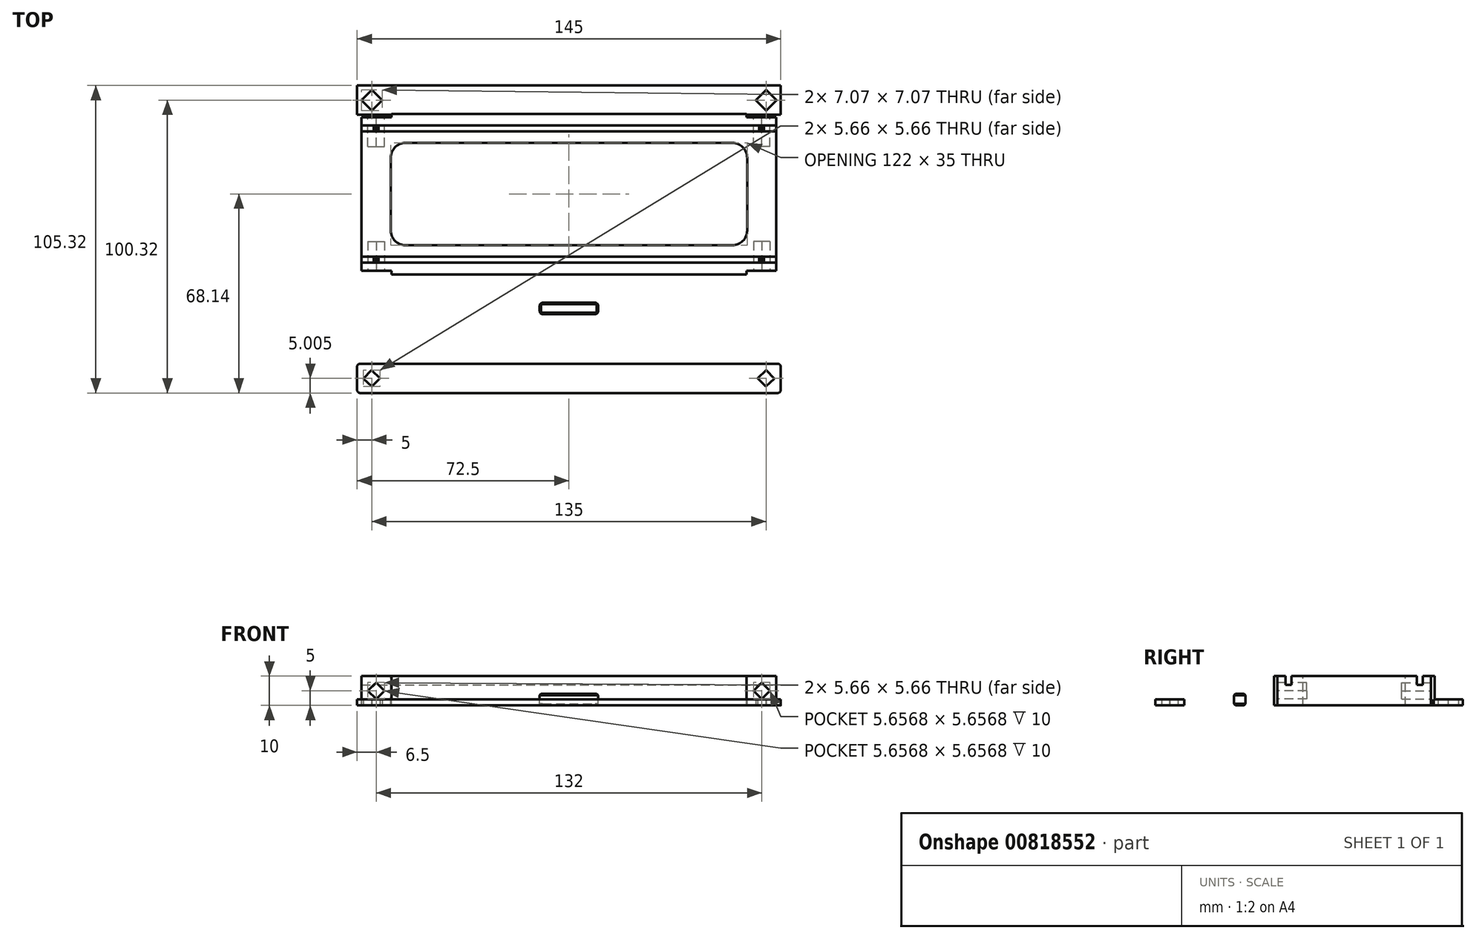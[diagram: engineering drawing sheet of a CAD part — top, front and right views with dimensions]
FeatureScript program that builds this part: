
annotation { "Feature Type Name" : "Feature", "Feature Type Description" : "" }
export const myFeature = defineFeature(function(context is Context, id is Id, definition is map)
    precondition{}
    {
        {
            var Q0;
            Q0=qCreatedBy(makeId("Top.planeOp"),FACE);
            var sketch = newSketch(context, id + "F0", { "sketchPlane" : qUnion([Q0])});
            skLineSegment(sketch, "E0.bottom", {"start": v(71, -27.5) * mm, "end": v(-71, -27.5) * mm});
            skLineSegment(sketch, "E0.top", {"start": v(71, 27.5) * mm, "end": v(-71, 27.5) * mm});
            skLineSegment(sketch, "E0.left", {"start": v(71, -27.5) * mm, "end": v(71, 27.5) * mm});
            skLineSegment(sketch, "E0.right", {"start": v(-71, -27.5) * mm, "end": v(-71, 27.5) * mm});
            skPoint(sketch, "E0.middle", {"position": v(0, 0) * mm});
            skSolve(sketch);
        }
        {
            var Q0;
            Q0 = qSketchRegion(id + "F0", true);
            extrude(context, id + "F1", {"entities" : qUnion([Q0]), "depth" : 10 * mm, "offsetDistance" : 25 * mm});
        }
        {
            var Q0;
            Q0=makeQuery(id+"F1.opExtrude","CAP_FACE",FACE,{"disambiguationData":[OSD([sQuery(id+"F0.wireOp",EDGE,"E0.bottom"),sQuery(id+"F0.wireOp",EDGE,"E0.top"),sQuery(id+"F0.wireOp",EDGE,"E0.left"),sQuery(id+"F0.wireOp",EDGE,"E0.right")])],"isStart":false});
            var sketch = newSketch(context, id + "F2", { "sketchPlane" : qUnion([Q0])});
            skLineSegment(sketch, "E1.bottom", {"start": v(-71, 23.5) * mm, "end": v(71, 23.5) * mm});
            skLineSegment(sketch, "E1.top", {"start": v(-71, 21.5) * mm, "end": v(71, 21.5) * mm});
            skLineSegment(sketch, "E1.left", {"start": v(-71, 23.5) * mm, "end": v(-71, 21.5) * mm});
            skLineSegment(sketch, "E1.right", {"start": v(71, 23.5) * mm, "end": v(71, 21.5) * mm});
            skLineSegment(sketch, "E2.MirrorCS", {"start": v(71, -23.5) * mm, "end": v(71, -21.5) * mm});
            skLineSegment(sketch, "E3.MirrorCS", {"start": v(-71, -23.5) * mm, "end": v(-71, -21.5) * mm});
            skLineSegment(sketch, "E4.MirrorCS", {"start": v(-71, -23.5) * mm, "end": v(71, -23.5) * mm});
            skLineSegment(sketch, "E5.MirrorCS", {"start": v(-71, -21.5) * mm, "end": v(71, -21.5) * mm});
            skSolve(sketch);
        }
        {
            var Q0;
            Q0 = qSketchRegion(id + "F2", true);
            extrude(context, id + "F3", {"entities" : qUnion([Q0]), "operationType" : NewBodyOperationType.REMOVE, "oppositeDirection" : true, "depth" : 3 * mm, "offsetDistance" : 25 * mm});
        }
        {
            var Q0;
            {var subQ0=sQuery(id+"F0.wireOp",EDGE,"E0.left");var subQ1=sQuery(id+"F0.wireOp",EDGE,"E0.right");Q0=makeQuery(id+"F3.boolean.opBoolean","SPLIT",FACE,{"disambiguationData":[TD([makeQuery(id+"F3.opExtrude","SWEPT_FACE",FACE,{"disambiguationData":[OSD([sQuery(id+"F2.wireOp",EDGE,"E1.top")])]})])],"derivedFrom":makeQuery(id+"F1.opExtrude","CAP_FACE",FACE,{"disambiguationData":[OSD([sQuery(id+"F0.wireOp",EDGE,"E0.bottom"),sQuery(id+"F0.wireOp",EDGE,"E0.top"),subQ0,subQ1])],"isStart":false})});}
            var sketch = newSketch(context, id + "F4", { "sketchPlane" : qUnion([Q0])});
            skLineSegment(sketch, "E6.bottom", {"start": v(61, -17.5) * mm, "end": v(-61, -17.5) * mm});
            skLineSegment(sketch, "E6.top", {"start": v(61, 17.5) * mm, "end": v(-61, 17.5) * mm});
            skLineSegment(sketch, "E6.left", {"start": v(61, -17.5) * mm, "end": v(61, 17.5) * mm});
            skLineSegment(sketch, "E6.right", {"start": v(-61, -17.5) * mm, "end": v(-61, 17.5) * mm});
            skPoint(sketch, "E6.middle", {"position": v(0, 0) * mm});
            skLineSegment(sketch, "E7.bottom", {"start": v(-71, -27.5) * mm, "end": v(-60.8, -27.5) * mm});
            skLineSegment(sketch, "E7.top", {"start": v(-71, -26.3) * mm, "end": v(-60.8, -26.3) * mm});
            skLineSegment(sketch, "E7.left", {"start": v(-71, -27.5) * mm, "end": v(-71, -26.3) * mm});
            skLineSegment(sketch, "E7.right", {"start": v(-60.8, -27.5) * mm, "end": v(-60.8, -26.3) * mm});
            skLineSegment(sketch, "E8.bottom", {"start": v(-71, 27.5) * mm, "end": v(-60.8, 27.5) * mm});
            skLineSegment(sketch, "E8.top", {"start": v(-71, 26.3) * mm, "end": v(-60.8, 26.3) * mm});
            skLineSegment(sketch, "E8.left", {"start": v(-71, 27.5) * mm, "end": v(-71, 26.3) * mm});
            skLineSegment(sketch, "E8.right", {"start": v(-60.8, 27.5) * mm, "end": v(-60.8, 26.3) * mm});
            skLineSegment(sketch, "E9.MirrorCS", {"start": v(71, 27.5) * mm, "end": v(60.8, 27.5) * mm});
            skLineSegment(sketch, "E10.MirrorCS", {"start": v(71, 26.3) * mm, "end": v(60.8, 26.3) * mm});
            skLineSegment(sketch, "E11.MirrorCS", {"start": v(60.8, 27.5) * mm, "end": v(60.8, 26.3) * mm});
            skLineSegment(sketch, "E12.MirrorCS", {"start": v(71, 27.5) * mm, "end": v(71, 26.3) * mm});
            skLineSegment(sketch, "E13.MirrorCS", {"start": v(71, -27.5) * mm, "end": v(71, -26.3) * mm});
            skLineSegment(sketch, "E14.MirrorCS", {"start": v(71, -26.3) * mm, "end": v(60.8, -26.3) * mm});
            skLineSegment(sketch, "E15.MirrorCS", {"start": v(71, -27.5) * mm, "end": v(60.8, -27.5) * mm});
            skLineSegment(sketch, "E16.MirrorCS", {"start": v(60.8, -27.5) * mm, "end": v(60.8, -26.3) * mm});
            skSolve(sketch);
        }
        {
            var Q0;
            Q0 = qSketchRegion(id + "F4", true);
            extrude(context, id + "F5", {"entities" : qUnion([Q0]), "operationType" : NewBodyOperationType.REMOVE, "endBound" : BoundingType.THROUGH_ALL, "oppositeDirection" : true, "depth" : 25 * mm, "offsetDistance" : 25 * mm});
        }
        {
            var Q0;
            Q0=makeQuery(id+"F5.boolean.opBoolean","COPY",FACE,{"derivedFrom":makeQuery(id+"F5.opExtrude","SWEPT_FACE",FACE,{"disambiguationData":[OSD([sQuery(id+"F4.wireOp",EDGE,"E7.top")])]})});
            var sketch = newSketch(context, id + "F6", { "sketchPlane" : qUnion([Q0])});
            skLineSegment(sketch, "E17", {"start": v(-71, 5) * mm, "end": v(-66, 5) * mm, "construction": true});
            skCircle(sketch, "E18.cCircle", {"center": v(-66, 5) * mm, "radius": 2 * mm, "construction": true});
            skLineSegment(sketch, "E18.0", {"start": v(-63.17, 5) * mm, "end": v(-66, 2.17) * mm});
            skLineSegment(sketch, "E18.1", {"start": v(-66, 2.17) * mm, "end": v(-68.83, 5) * mm});
            skLineSegment(sketch, "E18.2", {"start": v(-68.83, 5) * mm, "end": v(-66, 7.83) * mm});
            skLineSegment(sketch, "E18.3", {"start": v(-66, 7.83) * mm, "end": v(-63.17, 5) * mm});
            skPoint(sketch, "E18.0.midPoint", {"position": v(-64.59, 3.59) * mm});
            skLineSegment(sketch, "E19.MirrorCS", {"start": v(63.17, 5) * mm, "end": v(66, 2.17) * mm});
            skLineSegment(sketch, "E20.MirrorCS", {"start": v(68.83, 5) * mm, "end": v(66, 7.83) * mm});
            skLineSegment(sketch, "E21.MirrorCS", {"start": v(66, 2.17) * mm, "end": v(68.83, 5) * mm});
            skLineSegment(sketch, "E22.MirrorCS", {"start": v(66, 7.83) * mm, "end": v(63.17, 5) * mm});
            skLineSegment(sketch, "E23.MirrorCS", {"start": v(71, 5) * mm, "end": v(66, 5) * mm, "construction": true});
            skCircle(sketch, "E24.MirrorC", {"center": v(66, 5) * mm, "radius": 2 * mm, "construction": true});
            skPoint(sketch, "E25.MirrorP", {"position": v(64.59, 3.59) * mm});
            skSolve(sketch);
        }
        {
            var Q0;
            Q0 = qSketchRegion(id + "F6", true);
            extrude(context, id + "F7", {"entities" : qUnion([Q0]), "operationType" : NewBodyOperationType.REMOVE, "oppositeDirection" : true, "depth" : 10 * mm, "offsetDistance" : 25 * mm});
        }
        {
            var Q0;
            Q0=makeQuery(id+"F5.boolean.opBoolean","COPY",EDGE,{"derivedFrom":makeQuery(id+"F5.opExtrude","SWEPT_EDGE",EDGE,{"disambiguationData":[OSD([sQuery(id+"F4.wireOp",EDGE,"E6.bottom"),sQuery(id+"F4.wireOp",EDGE,"E6.right")])]})});
            var Q1;
            Q1=makeQuery(id+"F5.boolean.opBoolean","COPY",EDGE,{"derivedFrom":makeQuery(id+"F5.opExtrude","SWEPT_EDGE",EDGE,{"disambiguationData":[OSD([sQuery(id+"F4.wireOp",EDGE,"E6.top"),sQuery(id+"F4.wireOp",EDGE,"E6.right")])]})});
            var Q2;
            Q2=makeQuery(id+"F5.boolean.opBoolean","COPY",EDGE,{"derivedFrom":makeQuery(id+"F5.opExtrude","SWEPT_EDGE",EDGE,{"disambiguationData":[OSD([sQuery(id+"F4.wireOp",EDGE,"E6.top"),sQuery(id+"F4.wireOp",EDGE,"E6.left")])]})});
            var Q3;
            Q3=makeQuery(id+"F5.boolean.opBoolean","COPY",EDGE,{"derivedFrom":makeQuery(id+"F5.opExtrude","SWEPT_EDGE",EDGE,{"disambiguationData":[OSD([sQuery(id+"F4.wireOp",EDGE,"E6.bottom"),sQuery(id+"F4.wireOp",EDGE,"E6.left")])]})});
            fillet(context, id + "F8", {"entities" : qUnion([Q0, Q1, Q2, Q3]), "radius" : 5 * mm, "tangentPropagation" : true, "allowEdgeOverflow" : false});
        }
        {
            var Q0;
            Q0=qCreatedBy(makeId("Right.planeOp"),FACE);
            var sketch = newSketch(context, id + "F9", { "sketchPlane" : qUnion([Q0])});
            skLineSegment(sketch, "E26.bottom", {"start": v(-41.13, 0) * mm, "end": v(-37.23, 0) * mm});
            skLineSegment(sketch, "E26.top", {"start": v(-41.13, 3.9) * mm, "end": v(-37.23, 3.9) * mm});
            skLineSegment(sketch, "E26.left", {"start": v(-41.13, 0) * mm, "end": v(-41.13, 3.9) * mm});
            skLineSegment(sketch, "E26.right", {"start": v(-37.23, 0) * mm, "end": v(-37.23, 3.9) * mm});
            skSolve(sketch);
        }
        {
            var Q0;
            Q0 = qSketchRegion(id + "F9", true);
            extrude(context, id + "F10", {"entities" : qUnion([Q0]), "endBound" : BoundingType.SYMMETRIC, "depth" : 20 * mm, "offsetDistance" : 25 * mm});
        }
        {
            var Q0;
            Q0=makeQuery(id+"F10.opExtrude","CAP_EDGE",EDGE,{"disambiguationData":[OSD([sQuery(id+"F9.wireOp",EDGE,"E26.left")])],"isStart":false});
            var Q1;
            Q1=makeQuery(id+"F10.opExtrude","CAP_EDGE",EDGE,{"disambiguationData":[OSD([sQuery(id+"F9.wireOp",EDGE,"E26.right")])],"isStart":false});
            var Q2;
            Q2=makeQuery(id+"F10.opExtrude","CAP_EDGE",EDGE,{"disambiguationData":[OSD([sQuery(id+"F9.wireOp",EDGE,"E26.left")])],"isStart":true});
            var Q3;
            Q3=makeQuery(id+"F10.opExtrude","CAP_EDGE",EDGE,{"disambiguationData":[OSD([sQuery(id+"F9.wireOp",EDGE,"E26.right")])],"isStart":true});
            fillet(context, id + "F11", {"entities" : qUnion([Q0, Q1, Q2, Q3]), "radius" : 1 * mm, "tangentPropagation" : true, "allowEdgeOverflow" : false});
        }
        {
            var Q0;
            Q0=makeQuery(id+"F10.opExtrude","SWEPT_FACE",FACE,{"disambiguationData":[OSD([sQuery(id+"F9.wireOp",EDGE,"E26.top")])]});
            var Q1;
            Q1=makeQuery(id+"F10.opExtrude","SWEPT_FACE",FACE,{"disambiguationData":[OSD([sQuery(id+"F9.wireOp",EDGE,"E26.bottom")])]});
            chamfer(context, id + "F12", {"entities" : qUnion([Q0, Q1]), "width" : .5 * mm, "tangentPropagation" : true});
        }
        {
            var Q0;
            Q0=qCreatedBy(makeId("Top.planeOp"),FACE);
            var sketch = newSketch(context, id + "F13", { "sketchPlane" : qUnion([Q0])});
            skLineSegment(sketch, "E27.bottom", {"start": v(72.5, 27.18) * mm, "end": v(-72.5, 27.18) * mm});
            skLineSegment(sketch, "E27.top", {"start": v(72.5, 37.18) * mm, "end": v(-72.5, 37.18) * mm});
            skLineSegment(sketch, "E27.left", {"start": v(72.5, 27.18) * mm, "end": v(72.5, 37.18) * mm});
            skLineSegment(sketch, "E27.right", {"start": v(-72.5, 27.18) * mm, "end": v(-72.5, 37.18) * mm});
            skPoint(sketch, "E27.middle", {"position": v(0, 32.18) * mm});
            skLineSegment(sketch, "E28", {"start": v(-72.5, 32.18) * mm, "end": v(-67.5, 32.18) * mm, "construction": true});
            skCircle(sketch, "E29.cCircle", {"center": v(-67.5, 32.18) * mm, "radius": 2.5 * mm, "construction": true});
            skLineSegment(sketch, "E29.0", {"start": v(-63.96, 32.18) * mm, "end": v(-67.5, 28.64) * mm});
            skLineSegment(sketch, "E29.1", {"start": v(-67.5, 28.64) * mm, "end": v(-71.04, 32.18) * mm});
            skLineSegment(sketch, "E29.2", {"start": v(-71.04, 32.18) * mm, "end": v(-67.5, 35.72) * mm});
            skLineSegment(sketch, "E29.3", {"start": v(-67.5, 35.72) * mm, "end": v(-63.96, 32.18) * mm});
            skPoint(sketch, "E29.0.midPoint", {"position": v(-65.73, 30.41) * mm});
            skLineSegment(sketch, "E30.MirrorCS", {"start": v(67.5, 35.72) * mm, "end": v(63.96, 32.18) * mm});
            skLineSegment(sketch, "E31.MirrorCS", {"start": v(63.96, 32.18) * mm, "end": v(67.5, 28.64) * mm});
            skLineSegment(sketch, "E32.MirrorCS", {"start": v(67.5, 28.64) * mm, "end": v(71.04, 32.18) * mm});
            skLineSegment(sketch, "E33.MirrorCS", {"start": v(71.04, 32.18) * mm, "end": v(67.5, 35.72) * mm});
            skSolve(sketch);
        }
        {
            var Q0;
            Q0 = qSketchRegion(id + "F13", true);
            extrude(context, id + "F14", {"entities" : qUnion([Q0]), "depth" : 2 * mm, "offsetDistance" : 25 * mm});
        }
        {
            var Q0;
            Q0=makeQuery(id+"F5.boolean.opBoolean","COPY",FACE,{"derivedFrom":makeQuery(id+"F5.opExtrude","SWEPT_FACE",FACE,{"disambiguationData":[OSD([sQuery(id+"F4.wireOp",EDGE,"E8.top")])]})});
            var sketch = newSketch(context, id + "F15", { "sketchPlane" : qUnion([Q0])});
            skLineSegment(sketch, "E34.0", {"start": v(66, 7.83) * mm, "end": v(63.17, 5) * mm});
            skLineSegment(sketch, "E35.0", {"start": v(63.17, 5) * mm, "end": v(66, 2.17) * mm});
            skLineSegment(sketch, "E36.0", {"start": v(66, 2.17) * mm, "end": v(68.83, 5) * mm});
            skLineSegment(sketch, "E37.0", {"start": v(68.83, 5) * mm, "end": v(66, 7.83) * mm});
            skLineSegment(sketch, "E38.0", {"start": v(-68.83, 5) * mm, "end": v(-66, 7.83) * mm});
            skLineSegment(sketch, "E39.0", {"start": v(-66, 7.83) * mm, "end": v(-63.17, 5) * mm});
            skLineSegment(sketch, "E40.0", {"start": v(-63.17, 5) * mm, "end": v(-66, 2.17) * mm});
            skLineSegment(sketch, "E41.0", {"start": v(-66, 2.17) * mm, "end": v(-68.83, 5) * mm});
            skSolve(sketch);
        }
        {
            var Q0;
            Q0 = qSketchRegion(id + "F15", true);
            extrude(context, id + "F16", {"entities" : qUnion([Q0]), "operationType" : NewBodyOperationType.REMOVE, "oppositeDirection" : true, "depth" : 10 * mm, "offsetDistance" : 25 * mm});
        }
        {
            var Q0;
            Q0=qCreatedBy(makeId("Top.planeOp"),FACE);
            var sketch = newSketch(context, id + "F17", { "sketchPlane" : qUnion([Q0])});
            skLineSegment(sketch, "E42.bottom", {"start": v(72.5, -68.14) * mm, "end": v(-72.5, -68.14) * mm});
            skLineSegment(sketch, "E42.top", {"start": v(72.5, -58.14) * mm, "end": v(-72.5, -58.14) * mm});
            skLineSegment(sketch, "E42.left", {"start": v(72.5, -68.14) * mm, "end": v(72.5, -58.14) * mm});
            skLineSegment(sketch, "E42.right", {"start": v(-72.5, -68.14) * mm, "end": v(-72.5, -58.14) * mm});
            skPoint(sketch, "E42.middle", {"position": v(0, -63.14) * mm});
            skLineSegment(sketch, "E43", {"start": v(-72.5, -63.14) * mm, "end": v(72.5, -63.14) * mm, "construction": true});
            skCircle(sketch, "E44.cCircle", {"center": v(-67.5, -63.14) * mm, "radius": 2 * mm, "construction": true});
            skLineSegment(sketch, "E44.0", {"start": v(-64.67, -63.08) * mm, "end": v(-67.44, -65.96) * mm});
            skLineSegment(sketch, "E44.1", {"start": v(-67.44, -65.96) * mm, "end": v(-70.33, -63.2) * mm});
            skLineSegment(sketch, "E44.2", {"start": v(-70.33, -63.2) * mm, "end": v(-67.56, -60.3) * mm});
            skLineSegment(sketch, "E44.3", {"start": v(-67.56, -60.3) * mm, "end": v(-64.67, -63.08) * mm});
            skPoint(sketch, "E44.0.midPoint", {"position": v(-66.06, -64.52) * mm});
            skLineSegment(sketch, "E45.MirrorCS", {"start": v(67.56, -60.3) * mm, "end": v(64.67, -63.08) * mm});
            skCircle(sketch, "E46.MirrorC", {"center": v(67.5, -63.14) * mm, "radius": 2 * mm, "construction": true});
            skLineSegment(sketch, "E47.MirrorCS", {"start": v(70.33, -63.2) * mm, "end": v(67.56, -60.3) * mm});
            skLineSegment(sketch, "E48.MirrorCS", {"start": v(67.44, -65.96) * mm, "end": v(70.33, -63.2) * mm});
            skPoint(sketch, "E49.MirrorP", {"position": v(66.06, -64.52) * mm});
            skLineSegment(sketch, "E50.MirrorCS", {"start": v(64.67, -63.08) * mm, "end": v(67.44, -65.96) * mm});
            skSolve(sketch);
        }
        {
            var Q0;
            Q0 = qSketchRegion(id + "F17", true);
            extrude(context, id + "F18", {"entities" : qUnion([Q0]), "depth" : 2 * mm, "offsetDistance" : 25 * mm});
        }
        {
            var Q0;
            Q0=makeQuery(id+"F18.opExtrude","SWEPT_EDGE",EDGE,{"disambiguationData":[OSD([sQuery(id+"F17.wireOp",EDGE,"E42.bottom"),sQuery(id+"F17.wireOp",EDGE,"E42.right")])]});
            var Q1;
            Q1=makeQuery(id+"F18.opExtrude","SWEPT_EDGE",EDGE,{"disambiguationData":[OSD([sQuery(id+"F17.wireOp",EDGE,"E42.bottom"),sQuery(id+"F17.wireOp",EDGE,"E42.left")])]});
            var Q2;
            Q2=makeQuery(id+"F18.opExtrude","SWEPT_EDGE",EDGE,{"disambiguationData":[OSD([sQuery(id+"F17.wireOp",EDGE,"E42.top"),sQuery(id+"F17.wireOp",EDGE,"E42.left")])]});
            var Q3;
            Q3=makeQuery(id+"F18.opExtrude","SWEPT_EDGE",EDGE,{"disambiguationData":[OSD([sQuery(id+"F17.wireOp",EDGE,"E42.top"),sQuery(id+"F17.wireOp",EDGE,"E42.right")])]});
            fillet(context, id + "F19", {"entities" : qUnion([Q0, Q1, Q2, Q3]), "radius" : 1 * mm, "tangentPropagation" : true, "allowEdgeOverflow" : false});
        }
    });
